# Revit family: FU_Table_Sandler_Momo 1
name_source: partatom
category: Furniture
units: mm (PartAtom-declared; Revit-internal decimal feet)

## family parameters
Always vertical = Yes
Cut with Voids When Loaded = No
OmniClass Number = 23.40.20.00
OmniClass Title = General Furniture and Specialties
Room Calculation Point = No
Shared = No
Work Plane-Based = No

## types (4) — shared parameters
Height = 740 mm  [stored 2.42782 ft]
Manufacturer = Sandler
URL = https://www.sandlerseating.com
zero-valued in all types: Default Elevation

## per-type parameters (varying)
| type | Description | Frame | Top | Top Type |
| MOMO TABLE 1-600 | Dining height table base with 60cm / 24″ diameter folding top. The base is in steel treated with cataphoresis process. | Metal - Powdercoat - White NCS 0500-N | Metal - Powdercoat - White NCS 0500-N | FU_Table Top_Ta : 600mm Rnd Top |
| MOMO TABLE 1-700 | Dining height table base with 70cm / 28". The base is in steel treated with cataphoresis process. | Metal - Powdercoat - Senf - NCS 2070-Y10R | Metal - Powdercoat - Senf - NCS 2070-Y10R | FU_Table Top_Ta : 700mm Sqr Top |
| MOMO TABLE 1Q-600 | Dining height table base with 60cm x 60cm / 24″ x 24″ folding top. The base is in steel treated with cataphoresis process. | Metal - Powdercoat - Dark Green NCS 8010-G10Y | Metal - Powdercoat - Dark Green NCS 8010-G10Y | FU_Table Top_Ta-Q : 600mm Sqr Top |
| MOMO TABLE 1Q-700 | Dining height table base with 70cm x 70cm / 28″ x 28″ folding top. The base is in steel treated with cataphoresis process. | Metal - Powdercoat - Aubergine NCS 5540-Y90R | Metal - Powdercoat - Aubergine NCS 5540-Y90R | FU_Table Top_Ta-Q : 700mm Sqr Top |

note: column(s) folded — value = type name in every type: Model

note: [stored X ft] marks values corroborated as IEEE doubles in the binary element streams (Revit-internal decimal feet)

## geometry (parser evidence)
native form markers: Sweep x9
no freeform markers — native parametric forms only
